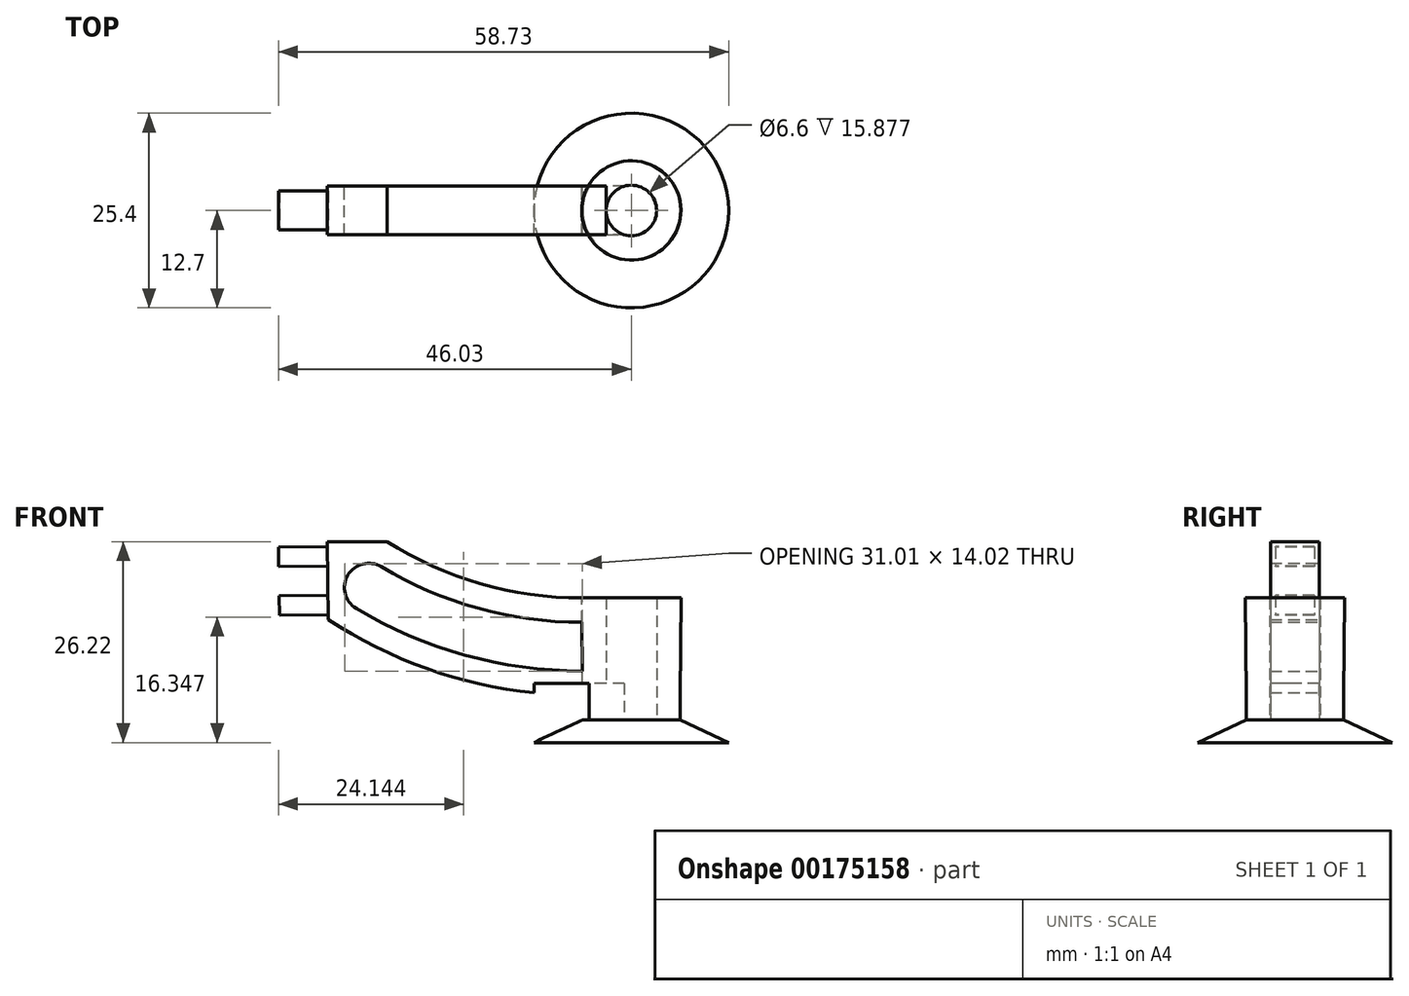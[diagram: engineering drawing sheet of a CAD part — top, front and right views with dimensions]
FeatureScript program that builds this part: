
annotation { "Feature Type Name" : "Feature", "Feature Type Description" : "" }
export const myFeature = defineFeature(function(context is Context, id is Id, definition is map)
    precondition{}
    {
        {
            var Q0;
            Q0=qCreatedBy(makeId("Front.planeOp"),FACE);
            var sketch = newSketch(context, id + "F0", { "sketchPlane" : qUnion([Q0])});
            skLineSegment(sketch, "E0", {"start": v(-6.48, 12.7) * mm, "end": v(-3.3, 12.7) * mm});
            skLineSegment(sketch, "E1", {"start": v(-3.3, 12.7) * mm, "end": v(-3.3, 0) * mm});
            skLineSegment(sketch, "E2", {"start": v(0, -6.16) * mm, "end": v(0, -3.17) * mm});
            skArc(sketch, "E3", {"start": v(-31.88, 20.06) * mm, "mid": v(-19.7, 14.58) * mm, "end": v(-6.48, 12.7) * mm});
            skArc(sketch, "E4", {"start": v(-39.56, 9.9) * mm, "mid": v(-23.68, 2.5) * mm, "end": v(-6.35, 0) * mm});
            skLineSegment(sketch, "E5", {"start": v(-31.88, 20.06) * mm, "end": v(-39.69, 20.06) * mm});
            skLineSegment(sketch, "E6", {"start": v(-6.35, 0) * mm, "end": v(-6.35, -3.2) * mm});
            skLineSegment(sketch, "E7", {"start": v(-6.35, 0) * mm, "end": v(-3.3, 0) * mm});
            skArc(sketch, "E8.0", {"start": v(-32.61, 16.78) * mm, "mid": v(-20.04, 11.37) * mm, "end": v(-6.48, 9.53) * mm});
            skArc(sketch, "E9.0", {"start": v(-35.89, 11.34) * mm, "mid": v(-21.74, 5.25) * mm, "end": v(-6.48, 3.17) * mm});
            skArc(sketch, "E10", {"start": v(-32.61, 16.78) * mm, "mid": v(-36.97, 15.7) * mm, "end": v(-35.89, 11.34) * mm});
            skLineSegment(sketch, "E11", {"start": v(-6.48, 12.7) * mm, "end": v(-6.35, 0) * mm});
            skLineSegment(sketch, "E12", {"start": v(-6.48, 9.53) * mm, "end": v(-3.3, 9.53) * mm});
            skLineSegment(sketch, "E13", {"start": v(-6.48, 3.17) * mm, "end": v(-3.3, 3.17) * mm});
            skLineSegment(sketch, "E14", {"start": v(0, -6.16) * mm, "end": v(-12.7, -6.16) * mm});
            skLineSegment(sketch, "E15", {"start": v(-12.7, -6.16) * mm, "end": v(-6.35, -3.2) * mm});
            skLineSegment(sketch, "E16", {"start": v(-3.3, 0) * mm, "end": v(-3.3, -3.17) * mm});
            skLineSegment(sketch, "E17", {"start": v(-3.3, -3.17) * mm, "end": v(0, -3.17) * mm});
            skLineSegment(sketch, "E18", {"start": v(-39.69, 20.06) * mm, "end": v(-39.56, 9.9) * mm});
            skSolve(sketch);
        }
        {
            var Q0;
            {var subQ2=sQuery(id+"F0.wireOp",EDGE,"E3");Q0=makeQuery(id+"F0.imprint","IMPRINT",FACE,{"disambiguationData":[TD([[makeQuery(id+"F0.imprint","IMPRINT",EDGE,{"derivedFrom":subQ2}),-1.0]])]});}
            var Q1;
            {var subQ0=sQuery(id+"F0.wireOp",EDGE,"E0");Q1=makeQuery(id+"F0.imprint","IMPRINT",FACE,{"disambiguationData":[TD([[makeQuery(id+"F0.imprint","IMPRINT",EDGE,{"derivedFrom":subQ0}),-1.0]])]});}
            var Q2;
            {var subQ0=sQuery(id+"F0.wireOp",EDGE,"E7");Q2=makeQuery(id+"F0.imprint","IMPRINT",FACE,{"disambiguationData":[TD([[makeQuery(id+"F0.imprint","IMPRINT",EDGE,{"derivedFrom":subQ0}),1.0]])]});}
            var Q3;
            {var subQ0=sQuery(id+"F0.wireOp",EDGE,"E12");Q3=makeQuery(id+"F0.imprint","IMPRINT",FACE,{"disambiguationData":[TD([[makeQuery(id+"F0.imprint","IMPRINT",EDGE,{"derivedFrom":subQ0}),-1.0]])]});}
            extrude(context, id + "F1", {"entities" : qUnion([Q0, Q1, Q2, Q3]), "endBound" : BoundingType.SYMMETRIC, "depth" : 6.35 * mm});
        }
        {
            var Q0;
            {var subQ2=sQuery(id+"F0.wireOp",EDGE,"E0");Q0=makeQuery(id+"F0.imprint","IMPRINT",FACE,{"disambiguationData":[TD([[makeQuery(id+"F0.imprint","IMPRINT",EDGE,{"derivedFrom":subQ2}),-1.0]])]});}
            var Q1;
            {var subQ0=sQuery(id+"F0.wireOp",EDGE,"E12");Q1=makeQuery(id+"F0.imprint","IMPRINT",FACE,{"disambiguationData":[TD([[makeQuery(id+"F0.imprint","IMPRINT",EDGE,{"derivedFrom":subQ0}),-1.0]])]});}
            var Q2;
            {var subQ0=sQuery(id+"F0.wireOp",EDGE,"E7");Q2=makeQuery(id+"F0.imprint","IMPRINT",FACE,{"disambiguationData":[TD([[makeQuery(id+"F0.imprint","IMPRINT",EDGE,{"derivedFrom":subQ0}),1.0]])]});}
            var Q3;
            {var subQ1=sQuery(id+"F0.wireOp",EDGE,"gUPBDrE7-IvuX-507v-aZ9k-2bwcfglypEaZ");Q3=makeQuery(id+"F0.imprint","IMPRINT",FACE,{"disambiguationData":[TD([[makeQuery(id+"F0.imprint","IMPRINT",EDGE,{"derivedFrom":subQ1}),1.0]])]});}
            var Q4;
            Q4=makeQuery(id+"F0.imprint","IMPRINT",FACE,{"disambiguationData":[TD([[makeQuery(id+"F0.imprint","IMPRINT",EDGE,{"derivedFrom":sQuery(id+"F0.wireOp",EDGE,"E2")}),1.0]])]});
            var Q5;
            Q5=sQuery(id+"F0.wireOp",EDGE,"E2");
            revolve(context, id + "F2", {"entities" : qUnion([Q0, Q1, Q2, Q3, Q4]), "axis" : qUnion([Q5]), "revolveType" : RevolveType.FULL});
        }
        {
            var Q0;
            Q0=makeQuery(id+"F1.opExtrude","SWEPT_FACE",FACE,{"disambiguationData":[OSD([sQuery(id+"F0.wireOp",EDGE,"E18")])]});
            var sketch = newSketch(context, id + "F3", { "sketchPlane" : qUnion([Q0])});
            skPoint(sketch, "E19", {"position": v(0, 15.47) * mm});
            skPoint(sketch, "E19.positionSnap0", {"position": v(0, 10.4) * mm});
            skPoint(sketch, "E19.positionSnap1", {"position": v(3.18, 15.47) * mm});
            skLineSegment(sketch, "E20.bottom", {"start": v(-2.54, 19.92) * mm, "end": v(2.54, 19.92) * mm});
            skLineSegment(sketch, "E20.top", {"start": v(-2.54, 11.03) * mm, "end": v(2.54, 11.03) * mm});
            skLineSegment(sketch, "E21", {"start": v(-2.54, 17.38) * mm, "end": v(2.54, 17.38) * mm});
            skLineSegment(sketch, "E22", {"start": v(-2.54, 13.57) * mm, "end": v(2.54, 13.57) * mm});
            skLineSegment(sketch, "E23", {"start": v(-2.54, 19.92) * mm, "end": v(-2.54, 17.38) * mm});
            skLineSegment(sketch, "E24", {"start": v(2.54, 19.92) * mm, "end": v(2.54, 17.38) * mm});
            skLineSegment(sketch, "E25", {"start": v(2.54, 13.57) * mm, "end": v(2.54, 11.03) * mm});
            skLineSegment(sketch, "E26", {"start": v(-2.54, 13.57) * mm, "end": v(-2.54, 11.03) * mm});
            skSolve(sketch);
        }
        {
            var Q0;
            {var subQ0=sQuery(id+"F3.wireOp",EDGE,"E20.bottom");Q0=makeQuery(id+"F3.imprint","IMPRINT",FACE,{"disambiguationData":[TD([[makeQuery(id+"F3.imprint","IMPRINT",EDGE,{"derivedFrom":subQ0}),-1.0]])]});}
            var Q1;
            {var subQ0=sQuery(id+"F3.wireOp",EDGE,"E20.top");Q1=makeQuery(id+"F3.imprint","IMPRINT",FACE,{"disambiguationData":[TD([[makeQuery(id+"F3.imprint","IMPRINT",EDGE,{"derivedFrom":subQ0}),1.0]])]});}
            extrude(context, id + "F4", {"entities" : qUnion([Q0, Q1]), "operationType" : NewBodyOperationType.ADD, "depth" : 6.35 * mm});
        }
        {
            var Q0;
            Q0=qCreatedBy(makeId("Right.planeOp"),FACE);
            cPlane(context, id + "F5", {"entities" : qUnion([Q0]), "cplaneType" : CPlaneType.OFFSET, "offset" : 6.35 * mm, "oppositeDirection" : true, "width" : 152.4 * mm, "height" : 152.4 * mm});
        }
        {
            var Q0;
            Q0=qCreatedBy(id+"F5.planeOp",FACE);
            var sketch = newSketch(context, id + "F6", { "sketchPlane" : qUnion([Q0])});
            skLineSegment(sketch, "E27", {"start": v(0, 0) * mm, "end": v(0, -3.18) * mm});
            skLineSegment(sketch, "E28", {"start": v(0, 0) * mm, "end": v(0, 1.59) * mm});
            skLineSegment(sketch, "E29", {"start": v(0, -3.18) * mm, "end": v(-3.18, -3.18) * mm});
            skLineSegment(sketch, "E30", {"start": v(-3.18, -3.18) * mm, "end": v(-3.18, 1.59) * mm});
            skLineSegment(sketch, "E31", {"start": v(-3.18, 1.59) * mm, "end": v(0, 1.59) * mm});
            skLineSegment(sketch, "E32", {"start": v(0, -3.18) * mm, "end": v(3.18, -3.18) * mm});
            skLineSegment(sketch, "E33", {"start": v(0, 1.59) * mm, "end": v(3.18, 1.59) * mm});
            skLineSegment(sketch, "E34", {"start": v(3.18, 1.59) * mm, "end": v(3.18, -3.18) * mm});
            skSolve(sketch);
        }
        {
            var Q0;
            Q0 = qSketchRegion(id + "F6", true);
            extrude(context, id + "F7", {"entities" : qUnion([Q0]), "operationType" : NewBodyOperationType.REMOVE, "endBound" : BoundingType.SYMMETRIC, "depth" : 12.7 * mm});
        }
    });
